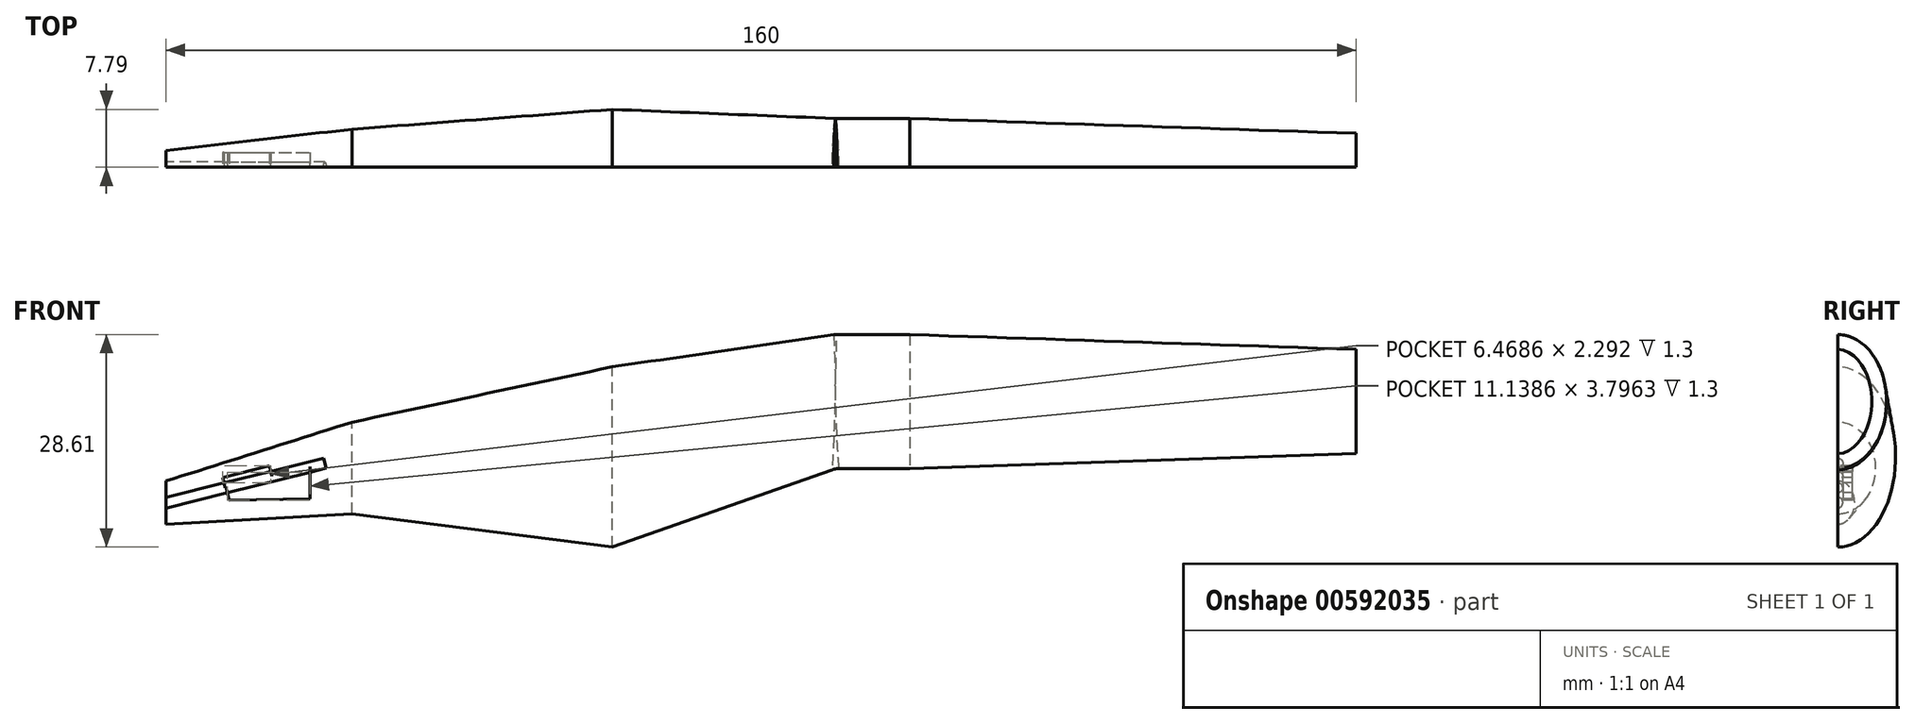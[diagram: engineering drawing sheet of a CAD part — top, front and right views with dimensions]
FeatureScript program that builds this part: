
annotation { "Feature Type Name" : "Feature", "Feature Type Description" : "" }
export const myFeature = defineFeature(function(context is Context, id is Id, definition is map)
    precondition{}
    {
        {
            var Q0;
            Q0=qCreatedBy(makeId("Right.planeOp"),FACE);
            var sketch = newSketch(context, id + "F0", { "sketchPlane" : qUnion([Q0])});
            skEllipse(sketch, "E0", {"center": v(0, 0) * mm, "majorRadius": 12.13 * mm, "minorRadius": 7.79 * mm, "majorAxis": v(0, -1)});
            skSolve(sketch);
        }
        {
            var Q0;
            Q0=qCreatedBy(makeId("Right.planeOp"),FACE);
            cPlane(context, id + "F1", {"entities" : qUnion([Q0]), "cplaneType" : CPlaneType.OFFSET, "offset" : 100 * mm, "width" : 150 * mm, "height" : 150 * mm});
        }
        {
            var Q0;
            Q0=qCreatedBy(id+"F1.planeOp",FACE);
            var sketch = newSketch(context, id + "F2", { "sketchPlane" : qUnion([Q0])});
            skEllipse(sketch, "E1", {"center": v(0, 7.46) * mm, "majorRadius": 9.02 * mm, "minorRadius": 6.57 * mm, "majorAxis": v(0, -1)});
            skSolve(sketch);
        }
        {
            var Q0;
            Q0=qCreatedBy(makeId("Right.planeOp"),FACE);
            cPlane(context, id + "F3", {"entities" : qUnion([Q0]), "cplaneType" : CPlaneType.OFFSET, "offset" : 35 * mm, "oppositeDirection" : true, "width" : 150 * mm, "height" : 150 * mm});
        }
        {
            var Q0;
            Q0=qCreatedBy(id+"F3.planeOp",FACE);
            var sketch = newSketch(context, id + "F4", { "sketchPlane" : qUnion([Q0])});
            skEllipse(sketch, "E2", {"center": v(0, -1.49) * mm, "majorRadius": 6.16 * mm, "minorRadius": 5.13 * mm, "majorAxis": v(0, -1)});
            skSolve(sketch);
        }
        {
            var Q0;
            Q0=qCreatedBy(makeId("Right.planeOp"),FACE);
            cPlane(context, id + "F5", {"entities" : qUnion([Q0]), "cplaneType" : CPlaneType.OFFSET, "offset" : 60 * mm, "oppositeDirection" : true, "width" : 150 * mm, "height" : 150 * mm});
        }
        {
            var Q0;
            Q0=qCreatedBy(id+"F5.planeOp",FACE);
            var sketch = newSketch(context, id + "F6", { "sketchPlane" : qUnion([Q0])});
            skEllipse(sketch, "E3", {"center": v(0, -6.15) * mm, "majorRadius": 2.9 * mm, "minorRadius": 2.28 * mm, "majorAxis": v(0, -1)});
            skSolve(sketch);
        }
        {
            var Q0;
            Q0=makeQuery(id+"F6.imprint","IMPRINT",FACE,{"disambiguationData":[TD([[makeQuery(id+"F6.imprint","IMPRINT",EDGE,{"derivedFrom":sQuery(id+"F6.wireOp",EDGE,"E3")}),1.0]])]});
            var Q1;
            Q1=makeQuery(id+"F4.imprint","IMPRINT",FACE,{"disambiguationData":[TD([[makeQuery(id+"F4.imprint","IMPRINT",EDGE,{"derivedFrom":sQuery(id+"F4.wireOp",EDGE,"E2")}),1.0]])]});
            loft(context, id + "F7", {"sheetProfilesArray" : [{ "sheetProfileEntities" : qUnion([Q0]) }, { "sheetProfileEntities" : qUnion([Q1]) }]});
        }
        {
            var Q1;
            Q1=makeQuery(id+"F0.imprint","IMPRINT",FACE,{"disambiguationData":[TD([[makeQuery(id+"F0.imprint","IMPRINT",EDGE,{"derivedFrom":sQuery(id+"F0.wireOp",EDGE,"E0")}),1.0]])]});
            var Q2;
            Q2=makeQuery(id+"F7.opLoft","CAP_FACE",FACE,{"disambiguationData":[OSD([makeQuery(id+"F4.imprint","IMPRINT",FACE,{"disambiguationData":[TD([[makeQuery(id+"F4.imprint","IMPRINT",EDGE,{"derivedFrom":sQuery(id+"F4.wireOp",EDGE,"E2")}),1.0]])]})])],"isStart":true});
            loft(context, id + "F8", {"operationType" : NewBodyOperationType.ADD, "sheetProfilesArray" : [{ "sheetProfileEntities" : qUnion([Q1]) }, { "sheetProfileEntities" : qUnion([Q2]) }]});
        }
        {
            var Q0;
            Q0=makeQuery(id+"F2.imprint","IMPRINT",FACE,{"disambiguationData":[TD([[makeQuery(id+"F2.imprint","IMPRINT",EDGE,{"derivedFrom":sQuery(id+"F2.wireOp",EDGE,"E1")}),1.0]])]});
            extrude(context, id + "F9", {"entities" : qUnion([Q0]), "oppositeDirection" : true, "depth" : 70 * mm, "offsetDistance" : 25 * mm});
        }
        {
            var Q0;
            Q0=makeQuery(id+"F8.opLoft","CAP_FACE",FACE,{"disambiguationData":[OSD([makeQuery(id+"F0.imprint","IMPRINT",FACE,{"disambiguationData":[TD([[makeQuery(id+"F0.imprint","IMPRINT",EDGE,{"derivedFrom":sQuery(id+"F0.wireOp",EDGE,"E0")}),1.0]])]})])],"isStart":true});
            var Q1;
            Q1=makeQuery(id+"F9.opExtrude","CAP_FACE",FACE,{"disambiguationData":[OSD([sQuery(id+"F2.wireOp",EDGE,"E1")])],"isStart":false});
            loft(context, id + "F10", {"operationType" : NewBodyOperationType.ADD, "sheetProfilesArray" : [{ "sheetProfileEntities" : qUnion([Q0]) }, { "sheetProfileEntities" : qUnion([Q1]) }]});
        }
        {
            var Q0;
            {var subQ0=sQuery(id+"F2.wireOp",EDGE,"E1");Q0=makeQuery(id+"F10.boolean.opBoolean","MERGE",EDGE,{"derivedFrom":[makeQuery(id+"F9.opExtrude","CAP_EDGE",EDGE,{"disambiguationData":[OSD([subQ0])],"isStart":false}),makeQuery(id+"F10.opLoft","MID_CAP_EDGE",EDGE,{"disambiguationData":[OSD([subQ0])],"capPos":1.0})]});}
            fillet(context, id + "F11", {"entities" : qUnion([Q0]), "radius" : 3 * mm, "tangentPropagation" : true, "allowEdgeOverflow" : false});
        }
        {
            var Q0;
            Q0=makeQuery(id+"F9.opExtrude","CAP_EDGE",EDGE,{"disambiguationData":[OSD([sQuery(id+"F2.wireOp",EDGE,"E1")])],"isStart":true});
            chamfer(context, id + "F12", {"entities" : qUnion([Q0]), "chamferType" : ChamferType.TWO_OFFSETS, "width1" : 2 * mm, "oppositeDirection" : false, "width2" : 60 * mm, "tangentPropagation" : true});
        }
        {
            var Q0;
            Q0=qCreatedBy(id+"F5.planeOp",FACE);
            var sketch = newSketch(context, id + "F13", { "sketchPlane" : qUnion([Q0])});
            skLineSegment(sketch, "E4.bottom", {"start": v(0, 26.84) * mm, "end": v(-15.83, 26.84) * mm});
            skLineSegment(sketch, "E4.top", {"start": v(0, -27.31) * mm, "end": v(-15.83, -27.31) * mm});
            skLineSegment(sketch, "E4.left", {"start": v(0, 26.84) * mm, "end": v(0, -27.31) * mm});
            skLineSegment(sketch, "E4.right", {"start": v(-15.83, 26.84) * mm, "end": v(-15.83, -27.31) * mm});
            skSolve(sketch);
        }
        {
            var Q0;
            Q0=makeQuery(id+"F13.imprint","IMPRINT",FACE,{"disambiguationData":[TD([[makeQuery(id+"F13.imprint","IMPRINT",EDGE,{"derivedFrom":sQuery(id+"F13.wireOp",EDGE,"E4.bottom")}),1.0]])]});
            extrude(context, id + "F14", {"entities" : qUnion([Q0]), "depth" : 170 * mm, "offsetDistance" : 25 * mm});
        }
        {
            var Q0;
            Q0=makeQuery(id+"F14.opExtrude","SWEPT_BODY",BODY,{"disambiguationData":[OSD([sQuery(id+"F13.wireOp",EDGE,"E4.bottom"),sQuery(id+"F13.wireOp",EDGE,"E4.top"),sQuery(id+"F13.wireOp",EDGE,"E4.left"),sQuery(id+"F13.wireOp",EDGE,"E4.right")])]});
            var Q1;
            Q1=makeQuery(id+"F7.opLoft","SWEPT_BODY",BODY,{"disambiguationData":[OSD([makeQuery(id+"F4.imprint","IMPRINT",FACE,{"disambiguationData":[TD([[makeQuery(id+"F4.imprint","IMPRINT",EDGE,{"derivedFrom":sQuery(id+"F4.wireOp",EDGE,"E2")}),1.0]])]}),makeQuery(id+"F6.imprint","IMPRINT",FACE,{"disambiguationData":[TD([[makeQuery(id+"F6.imprint","IMPRINT",EDGE,{"derivedFrom":sQuery(id+"F6.wireOp",EDGE,"E3")}),1.0]])]})])]});
            booleanBodies(context, id + "F15", {"operationType" : BooleanOperationType.SUBTRACTION, "tools" : qUnion([Q0]), "targets" : qUnion([Q1])});
        }
        {
            var Q0;
            Q0=makeQuery(id+"F15.opBoolean","COPY",FACE,{"derivedFrom":makeQuery(id+"F14.opExtrude","SWEPT_FACE",FACE,{"disambiguationData":[OSD([sQuery(id+"F13.wireOp",EDGE,"E4.left")])]})});
            var sketch = newSketch(context, id + "F16", { "sketchPlane" : qUnion([Q0])});
            skLineSegment(sketch, "E5", {"start": v(-84.18, -12.17) * mm, "end": v(-20.52, 3.68) * mm, "construction": true});
            skLineSegment(sketch, "E6", {"start": v(-60, -6.15) * mm, "end": v(-38.65, -0.84) * mm});
            skLineSegment(sketch, "E7", {"start": v(-60, -5.43) * mm, "end": v(-38.82, -0.16) * mm});
            skLineSegment(sketch, "E8", {"start": v(-38.82, -0.16) * mm, "end": v(-38.65, -0.84) * mm});
            skLineSegment(sketch, "E9", {"start": v(-60, -6.87) * mm, "end": v(-38.48, -1.52) * mm});
            skLineSegment(sketch, "E10", {"start": v(-38.48, -1.52) * mm, "end": v(-38.65, -0.84) * mm});
            skLineSegment(sketch, "E11", {"start": v(-52.22, -3.5) * mm, "end": v(-52.4, -2.77) * mm});
            skLineSegment(sketch, "E12", {"start": v(-52.4, -2.77) * mm, "end": v(-46.12, -1.2) * mm});
            skLineSegment(sketch, "E13", {"start": v(-46.12, -1.2) * mm, "end": v(-45.93, -1.93) * mm});
            skLineSegment(sketch, "E14", {"start": v(-51.75, -4.82) * mm, "end": v(-51.5, -5.84) * mm});
            skLineSegment(sketch, "E15", {"start": v(-51.5, -5.84) * mm, "end": v(-40.62, -5.65) * mm});
            skLineSegment(sketch, "E16", {"start": v(-40.62, -5.65) * mm, "end": v(-40.62, -2.05) * mm});
            skSolve(sketch);
        }
        {
            var Q0;
            {var subQ0=sQuery(id+"F16.wireOp",EDGE,"E6");Q0=makeQuery(id+"F16.imprint","IMPRINT",FACE,{"disambiguationData":[TD([[makeQuery(id+"F16.imprint","IMPRINT",EDGE,{"derivedFrom":subQ0}),1.0]])]});}
            var Q1;
            {var subQ0=sQuery(id+"F16.wireOp",EDGE,"E6");Q1=makeQuery(id+"F16.imprint","IMPRINT",FACE,{"disambiguationData":[TD([[makeQuery(id+"F16.imprint","IMPRINT",EDGE,{"derivedFrom":subQ0}),-1.0]])]});}
            extrude(context, id + "F17", {"entities" : qUnion([Q0, Q1]), "operationType" : NewBodyOperationType.REMOVE, "oppositeDirection" : true, "depth" : 0.7 * mm, "offsetDistance" : 25 * mm});
        }
        {
            var Q0;
            {var subQ0=sQuery(id+"F16.wireOp",EDGE,"E11");Q0=makeQuery(id+"F16.imprint","IMPRINT",FACE,{"disambiguationData":[TD([[makeQuery(id+"F16.imprint","IMPRINT",EDGE,{"derivedFrom":subQ0}),-1.0]])]});}
            var Q1;
            {var subQ0=sQuery(id+"F16.wireOp",EDGE,"E14");Q1=makeQuery(id+"F16.imprint","IMPRINT",FACE,{"disambiguationData":[TD([[makeQuery(id+"F16.imprint","IMPRINT",EDGE,{"derivedFrom":subQ0}),1.0]])]});}
            extrude(context, id + "F18", {"entities" : qUnion([Q0, Q1]), "operationType" : NewBodyOperationType.REMOVE, "oppositeDirection" : true, "depth" : 2 * mm, "offsetDistance" : 25 * mm});
        }
        {
            var Q0;
            {var subQ0=sQuery(id+"F16.wireOp",EDGE,"E7");var subQ1=makeQuery(id+"F17.boolean.opBoolean","COPY",FACE,{"derivedFrom":makeQuery(id+"F17.opExtrude","SWEPT_FACE",FACE,{"disambiguationData":[OSD([subQ0])]})});var subQ2=makeQuery(id+"F17.boolean.opBoolean","COPY",FACE,{"derivedFrom":makeQuery(id+"F17.opExtrude","CAP_FACE",FACE,{"disambiguationData":[OSD([sQuery(id+"F13.wireOp",EDGE,"E4.left"),subQ0,sQuery(id+"F16.wireOp",EDGE,"E8"),sQuery(id+"F16.wireOp",EDGE,"E9"),sQuery(id+"F16.wireOp",EDGE,"E10")])],"isStart":false})});Q0=makeQuery(id+"F18.boolean.opBoolean","SPLIT",EDGE,{"disambiguationData":[topologyDisambiguationEdgeConnected([subQ1,subQ2]),TD([makeQuery(id+"F7.opLoft","CAP_FACE",FACE,{"disambiguationData":[OSD([makeQuery(id+"F6.imprint","IMPRINT",FACE,{"disambiguationData":[TD([[makeQuery(id+"F6.imprint","IMPRINT",EDGE,{"derivedFrom":sQuery(id+"F6.wireOp",EDGE,"E3")}),1.0]])]})])],"isStart":true})])],"derivedFrom":makeQuery(id+"F17.boolean.opBoolean","COPY",EDGE,{"derivedFrom":makeQuery(id+"F17.opExtrude","CAP_EDGE",EDGE,{"disambiguationData":[OSD([subQ0])],"isStart":false})})});}
            var Q1;
            {var subQ0=sQuery(id+"F16.wireOp",EDGE,"E10");var subQ1=sQuery(id+"F16.wireOp",EDGE,"E8");var subQ2=sQuery(id+"F16.wireOp",EDGE,"E7");var subQ3=makeQuery(id+"F17.boolean.opBoolean","COPY",FACE,{"derivedFrom":makeQuery(id+"F17.opExtrude","CAP_FACE",FACE,{"disambiguationData":[OSD([sQuery(id+"F13.wireOp",EDGE,"E4.left"),subQ2,subQ1,sQuery(id+"F16.wireOp",EDGE,"E9"),subQ0])],"isStart":false})});var subQ4=makeQuery(id+"F17.boolean.opBoolean","COPY",FACE,{"derivedFrom":makeQuery(id+"F17.opExtrude","SWEPT_FACE",FACE,{"disambiguationData":[OSD([subQ2])]})});Q1=makeQuery(id+"F18.boolean.opBoolean","SPLIT",EDGE,{"disambiguationData":[topologyDisambiguationEdgeConnected([subQ4,subQ3]),TD([makeQuery(id+"F18.opExtrude","SWEPT_FACE",FACE,{"disambiguationData":[OSD([sQuery(id+"F16.wireOp",EDGE,"E13")])]})])],"derivedFrom":makeQuery(id+"F17.boolean.opBoolean","COPY",EDGE,{"derivedFrom":makeQuery(id+"F17.opExtrude","CAP_EDGE",EDGE,{"disambiguationData":[OSD([subQ2])],"isStart":false})})});}
            var Q2;
            {var subQ0=sQuery(id+"F16.wireOp",EDGE,"E9");var subQ1=makeQuery(id+"F17.boolean.opBoolean","COPY",FACE,{"derivedFrom":makeQuery(id+"F17.opExtrude","SWEPT_FACE",FACE,{"disambiguationData":[OSD([subQ0])]})});var subQ2=sQuery(id+"F16.wireOp",EDGE,"E10");var subQ3=sQuery(id+"F16.wireOp",EDGE,"E8");var subQ4=makeQuery(id+"F17.boolean.opBoolean","COPY",FACE,{"derivedFrom":makeQuery(id+"F17.opExtrude","CAP_FACE",FACE,{"disambiguationData":[OSD([sQuery(id+"F13.wireOp",EDGE,"E4.left"),sQuery(id+"F16.wireOp",EDGE,"E7"),subQ3,subQ0,subQ2])],"isStart":false})});Q2=makeQuery(id+"F18.boolean.opBoolean","SPLIT",EDGE,{"disambiguationData":[topologyDisambiguationEdgeConnected([subQ4,subQ1]),TD([makeQuery(id+"F18.opExtrude","SWEPT_FACE",FACE,{"disambiguationData":[OSD([sQuery(id+"F16.wireOp",EDGE,"E16")])]})])],"derivedFrom":makeQuery(id+"F17.boolean.opBoolean","COPY",EDGE,{"derivedFrom":makeQuery(id+"F17.opExtrude","CAP_EDGE",EDGE,{"disambiguationData":[OSD([subQ0])],"isStart":false})})});}
            var Q3;
            {var subQ0=sQuery(id+"F16.wireOp",EDGE,"E9");var subQ1=makeQuery(id+"F17.boolean.opBoolean","COPY",FACE,{"derivedFrom":makeQuery(id+"F17.opExtrude","SWEPT_FACE",FACE,{"disambiguationData":[OSD([subQ0])]})});var subQ2=makeQuery(id+"F17.boolean.opBoolean","COPY",FACE,{"derivedFrom":makeQuery(id+"F17.opExtrude","CAP_FACE",FACE,{"disambiguationData":[OSD([sQuery(id+"F13.wireOp",EDGE,"E4.left"),sQuery(id+"F16.wireOp",EDGE,"E7"),sQuery(id+"F16.wireOp",EDGE,"E8"),subQ0,sQuery(id+"F16.wireOp",EDGE,"E10")])],"isStart":false})});Q3=makeQuery(id+"F18.boolean.opBoolean","SPLIT",EDGE,{"disambiguationData":[topologyDisambiguationEdgeConnected([subQ2,subQ1]),TD([makeQuery(id+"F7.opLoft","CAP_FACE",FACE,{"disambiguationData":[OSD([makeQuery(id+"F6.imprint","IMPRINT",FACE,{"disambiguationData":[TD([[makeQuery(id+"F6.imprint","IMPRINT",EDGE,{"derivedFrom":sQuery(id+"F6.wireOp",EDGE,"E3")}),1.0]])]})])],"isStart":true})])],"derivedFrom":makeQuery(id+"F17.boolean.opBoolean","COPY",EDGE,{"derivedFrom":makeQuery(id+"F17.opExtrude","CAP_EDGE",EDGE,{"disambiguationData":[OSD([subQ0])],"isStart":false})})});}
            fillet(context, id + "F19", {"entities" : qUnion([Q0, Q1, Q2, Q3]), "radius" : 0.7 * mm, "tangentPropagation" : true, "allowEdgeOverflow" : false});
        }
    });
